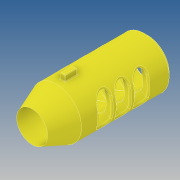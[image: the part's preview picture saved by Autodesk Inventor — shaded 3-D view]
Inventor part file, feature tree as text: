
AUTODESK INVENTOR PART (.ipt)
format: ipt  version: 2019 (Build 230136000, 136)  size: 680,960 bytes
history: native  units: mm
features: other x5, sketch x3, extrude x2, fillet x1, pattern_linear x1, mirror x1, chamfer x1
ambient origin geometry x8: Origin, YZ Plane, XZ Plane, XY Plane, X Axis, Y Axis, Z Axis, Center Point
bodies: Solide1 (feature_tree)
feature tree (14):
  other  "Révolution1"
  other  "Plan de construction7"
  extrude  "Extrusion11"  Depth=0.25mm
  fillet  "Congé3"  Radius=25.0mm
  pattern_linear  "Réseau rectangulaire5"  Count1=2  [1 undecoded]
  mirror  "Symétrie5"
  other  "Plan de construction9"
  extrude  "Extrusion14"  Depth=30.0mm
  chamfer  "Chanfrein4"  Distance=25.0mm
  sketch  "Esquisse1"
  other  "Plan de construction6"
  sketch  "Esquisse14"
  sketch  "Esquisse17"
  other  "Projeter les arêtes coupées7"
note: 1 required parameter value undecoded (feature->parameter linkage not recoverable at this tier; creation-order binding heuristic only, values carry confidence <= 0.55)
